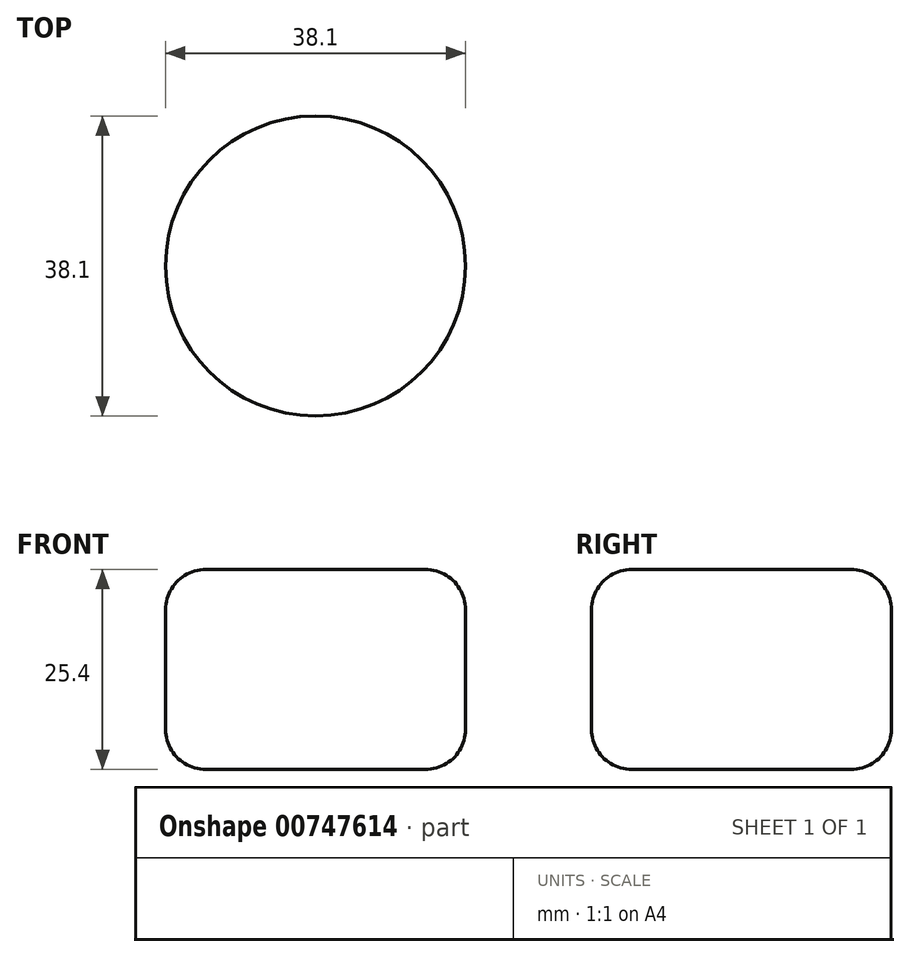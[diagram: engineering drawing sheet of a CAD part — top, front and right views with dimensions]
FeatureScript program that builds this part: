
annotation { "Feature Type Name" : "Feature", "Feature Type Description" : "" }
export const myFeature = defineFeature(function(context is Context, id is Id, definition is map)
    precondition{}
    {
        {
            var Q0;
            Q0=qCreatedBy(makeId("Top.planeOp"),FACE);
            var sketch = newSketch(context, id + "F0", { "sketchPlane" : qUnion([Q0])});
            skCircle(sketch, "E0", {"center": v(0, 0) * mm, "radius": 19.05 * mm});
            skSolve(sketch);
        }
        {
            var Q0;
            Q0=makeQuery(id+"F0.imprint","IMPRINT",FACE,{"disambiguationData":[TD([[makeQuery(id+"F0.imprint","IMPRINT",EDGE,{"derivedFrom":sQuery(id+"F0.wireOp",EDGE,"E0")}),1.0]])]});
            extrude(context, id + "F1", {"entities" : qUnion([Q0]), "depth" : 25.4 * mm, "offsetDistance" : 25.4 * mm});
        }
        {
            var Q0;
            Q0=makeQuery(id+"F1.opExtrude","CAP_EDGE",EDGE,{"disambiguationData":[OSD([sQuery(id+"F0.wireOp",EDGE,"E0")])],"isStart":true});
            var Q1;
            Q1=makeQuery(id+"F1.opExtrude","CAP_EDGE",EDGE,{"disambiguationData":[OSD([sQuery(id+"F0.wireOp",EDGE,"E0")])],"isStart":false});
            fillet(context, id + "F2", {"entities" : qUnion([Q0, Q1]), "radius" : 5.08 * mm, "tangentPropagation" : true, "allowEdgeOverflow" : false});
        }
    });
